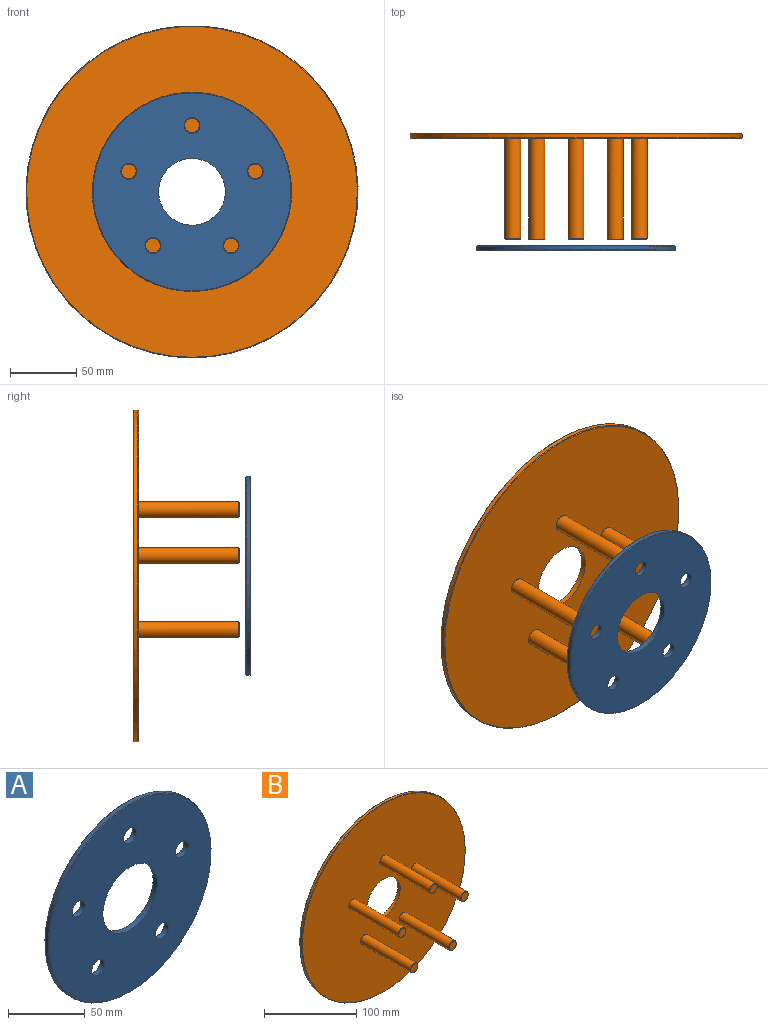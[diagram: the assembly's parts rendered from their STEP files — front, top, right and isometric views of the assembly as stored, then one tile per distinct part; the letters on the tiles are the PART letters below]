
ASSEMBLY  parts=2 mates=1
PART A: 11 faces, bbox 150x4x150 mm
  f0: cylinder r=25.1mm len=50.2mm, axis (0,1,0), area 630.8mm2, adj f7,f8
  f1: cylinder r=6mm len=12mm, axis (0,1,0), area 150.8mm2, adj f7,f8
  f2: cylinder r=6mm len=12mm, axis (0,1,0), area 150.8mm2, adj f7,f8
  f3: cylinder r=6mm len=12mm, axis (0,1,0), area 150.8mm2, adj f7,f8
  f4: cylinder r=6mm len=12mm, axis (0,1,0), area 150.8mm2, adj f7,f8
  f5: cylinder r=6mm len=12mm, axis (0,1,0), area 150.8mm2, adj f7,f8
  f6: cylinder r=75mm len=150mm, axis (0,1,0), area 1413.7mm2, adj f9,f10
  f7: plane 149x149mm, normal (0,-1,0), area 14891.9mm2, adj f0,f1,f2,f3,f4,f5,f10
  f8: plane 149x149mm, normal (0,1,0), area 14891.9mm2, adj f0,f1,f2,f3,f4,f5,f9
  f9: cone r=75mm half-angle=45deg, axis (0,-1,0), area 332.1mm2, adj f6,f8
  f10: cone r=74.5mm half-angle=45deg, axis (0,1,0), area 332.1mm2, adj f6,f7
PART B: 21 faces, bbox 250x80x250 mm
  f0: cylinder r=25.1mm len=50.2mm, axis (0,1,0), area 630.8mm2, adj f2,f3
  f1: cylinder r=125mm len=250mm, axis (0,1,0), area 2356.2mm2, adj f14,f15
  f2: plane 249x249mm, normal (0,-1,0), area 46150.8mm2, adj f0,f4,f6,f8,f10,f12,f15
  f3: plane 249x249mm, normal (0,1,0), area 46716.2mm2, adj f0,f14
  f4: cylinder r=6mm len=75.5mm, axis (0,1,0), area 2846.3mm2, adj f2,f16
  f5: plane 11x11mm, normal (0,-1,0), area 95mm2, adj f16
  f6: cylinder r=6mm len=75.5mm, axis (0,1,0), area 2846.3mm2, adj f2,f19
  f7: plane 11x11mm, normal (0,-1,0), area 95mm2, adj f19
  f8: cylinder r=6mm len=75.5mm, axis (0,1,0), area 2846.3mm2, adj f2,f20
  f9: plane 11x11mm, normal (0,-1,0), area 95mm2, adj f20
  f10: cylinder r=6mm len=75.5mm, axis (0,1,0), area 2846.3mm2, adj f2,f18
  f11: plane 11x11mm, normal (0,-1,0), area 95mm2, adj f18
  f12: cylinder r=6mm len=75.5mm, axis (0,1,0), area 2846.3mm2, adj f2,f17
  f13: plane 11x11mm, normal (0,-1,0), area 95mm2, adj f17
  f14: cone r=125mm half-angle=45deg, axis (0,-1,0), area 554.2mm2, adj f1,f3
  f15: cone r=124.5mm half-angle=45deg, axis (0,1,0), area 554.2mm2, adj f1,f2
  f16: cone r=5.5mm half-angle=45deg, axis (0,1,0), area 25.5mm2, adj f4,f5
  f17: cone r=5.5mm half-angle=45deg, axis (0,1,0), area 25.5mm2, adj f12,f13
  f18: cone r=5.5mm half-angle=45deg, axis (0,1,0), area 25.5mm2, adj f10,f11
  f19: cone r=5.5mm half-angle=45deg, axis (0,1,0), area 25.5mm2, adj f6,f7
  f20: cone r=5.5mm half-angle=45deg, axis (0,1,0), area 25.5mm2, adj f8,f9
PLACE A t=(0,-84.38,0)mm
PLACE B at identity
MATE slider A.f1 <-> B.f4  axis (0,-1,0) through (0,-88.38,50)mm
